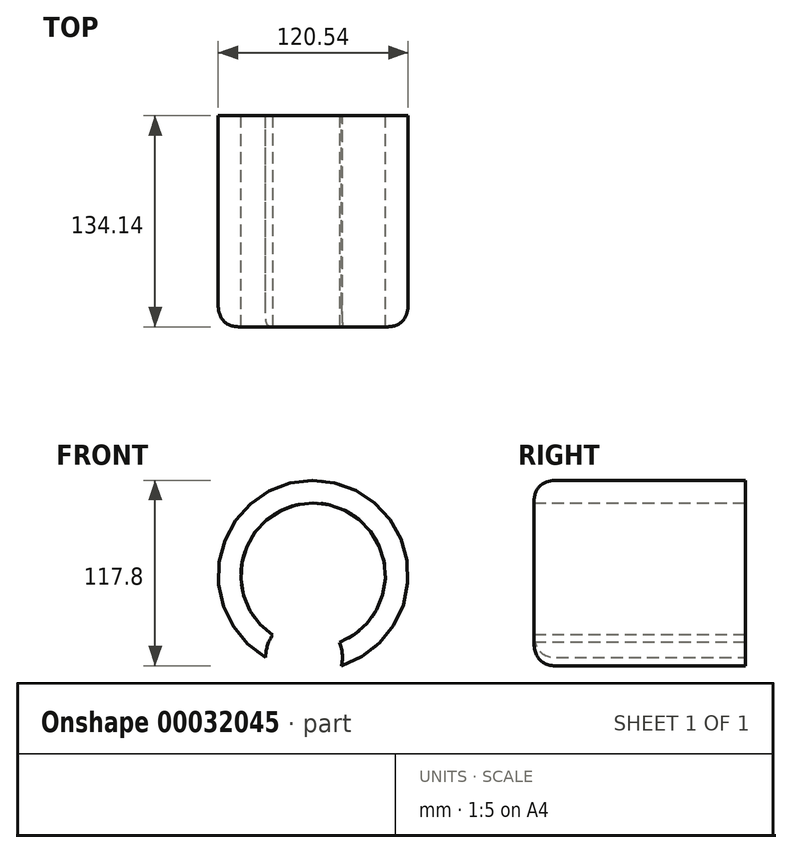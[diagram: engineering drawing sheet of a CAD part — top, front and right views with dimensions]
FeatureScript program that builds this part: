
annotation { "Feature Type Name" : "Feature", "Feature Type Description" : "" }
export const myFeature = defineFeature(function(context is Context, id is Id, definition is map)
    precondition{}
    {
        {
            var Q0;
            Q0=qCreatedBy(makeId("Front.planeOp"),FACE);
            var sketch = newSketch(context, id + "F0", { "sketchPlane" : qUnion([Q0])});
            skCircle(sketch, "E0", {"center": v(0, 0) * mm, "radius": 60.27 * mm});
            skSolve(sketch);
        }
        {
            var Q0;
            Q0=makeQuery(id+"F0.imprint","IMPRINT",FACE,{"disambiguationData":[TD([[makeQuery(id+"F0.imprint","IMPRINT",EDGE,{"derivedFrom":sQuery(id+"F0.wireOp",EDGE,"E0")}),1.0]])]});
            extrude(context, id + "F1", {"entities" : qUnion([Q0]), "depth" : 134.14 * mm});
        }
        {
            var Q0;
            Q0=makeQuery(id+"F1.opExtrude","CAP_EDGE",EDGE,{"disambiguationData":[OSD([sQuery(id+"F0.wireOp",EDGE,"E0")])],"isStart":false});
            fillet(context, id + "F2", {"entities" : qUnion([Q0]), "radius" : 14.4 * mm, "tangentPropagation" : true, "rho" : 0.5, "crossSection" : FilletCrossSection.CONIC, "allowEdgeOverflow" : false});
        }
        {
            var Q0;
            Q0=makeQuery(id+"F1.opExtrude","CAP_FACE",FACE,{"disambiguationData":[OSD([sQuery(id+"F0.wireOp",EDGE,"E0")])],"isStart":false});
            var sketch = newSketch(context, id + "F3", { "sketchPlane" : qUnion([Q0])});
            skLineSegment(sketch, "E1.bottom", {"start": v(-20.42, -26.64) * mm, "end": v(20.28, -26.64) * mm});
            skLineSegment(sketch, "E1.top", {"start": v(-20.42, 0) * mm, "end": v(20.28, 0) * mm});
            skLineSegment(sketch, "E1.left", {"start": v(-20.42, -26.64) * mm, "end": v(-20.42, 0) * mm});
            skLineSegment(sketch, "E1.right", {"start": v(20.28, -26.64) * mm, "end": v(20.28, 0) * mm});
            skSolve(sketch);
        }
        {
            var Q0;
            Q0=makeQuery(id+"F3.imprint","IMPRINT",FACE,{"disambiguationData":[TD([[makeQuery(id+"F3.imprint","IMPRINT",EDGE,{"derivedFrom":sQuery(id+"F3.wireOp",EDGE,"E1.bottom")}),1.0]])]});
            extrude(context, id + "F4", {"entities" : qUnion([Q0]), "operationType" : NewBodyOperationType.REMOVE, "oppositeDirection" : true, "depth" : 156.47 * mm});
        }
        {
            var Q0;
            Q0=makeQuery(id+"F1.opExtrude","CAP_FACE",FACE,{"disambiguationData":[OSD([sQuery(id+"F0.wireOp",EDGE,"E0")])],"isStart":false});
            extrude(context, id + "F5", {"entities" : qUnion([Q0]), "operationType" : NewBodyOperationType.REMOVE, "oppositeDirection" : true, "depth" : 234.53 * mm});
        }
        {
            var Q0;
            Q0=makeQuery(id+"F1.opExtrude","CAP_FACE",FACE,{"disambiguationData":[OSD([sQuery(id+"F0.wireOp",EDGE,"E0")])],"isStart":true});
            var sketch = newSketch(context, id + "F6", { "sketchPlane" : qUnion([Q0])});
            skCircle(sketch, "E2", {"center": v(5.77, -51.96) * mm, "radius": 24.38 * mm});
            skSolve(sketch);
        }
        {
            var Q0;
            {var subQ0=makeQuery(id+"F1.opExtrude","CAP_EDGE",EDGE,{"disambiguationData":[OSD([sQuery(id+"F0.wireOp",EDGE,"E0")])],"isStart":true});var subQ1=sQuery(id+"F6.wireOp",EDGE,"E2");var subQ3=makeQuery(id+"F6.imprint","INTERSECT",VERTEX,{"disambiguationData":[OD(0.0)],"derivedFrom":[subQ0,subQ1]});Q0=makeQuery(id+"F6.imprint","IMPRINT",FACE,{"disambiguationData":[TD([[makeQuery(id+"F6.imprint","IMPRINT",EDGE,{"disambiguationData":[TD([[subQ3,-1.0]])],"derivedFrom":subQ1}),1.0]])]});}
            var Q1;
            {var subQ0=sQuery(id+"F0.wireOp",EDGE,"E0");var subQ1=makeQuery(id+"F5.boolean.opBoolean","INTERSECT",EDGE,{"derivedFrom":[makeQuery(id+"F1.opExtrude","CAP_FACE",FACE,{"disambiguationData":[OSD([subQ0])],"isStart":true}),makeQuery(id+"F5.opExtrude","SWEPT_FACE",FACE,{"disambiguationData":[OSD([subQ0])]})]});var subQ2=sQuery(id+"F6.wireOp",EDGE,"E2");var subQ4=makeQuery(id+"F6.imprint","INTERSECT",VERTEX,{"disambiguationData":[OD(0.0)],"derivedFrom":[subQ1,subQ2]});Q1=makeQuery(id+"F6.imprint","IMPRINT",FACE,{"disambiguationData":[TD([[makeQuery(id+"F6.imprint","IMPRINT",EDGE,{"disambiguationData":[TD([[subQ4,1.0]])],"derivedFrom":subQ2}),1.0]])]});}
            var Q2;
            {var subQ0=sQuery(id+"F0.wireOp",EDGE,"E0");var subQ2=sQuery(id+"F6.wireOp",EDGE,"E2");var subQ5=makeQuery(id+"F1.opExtrude","CAP_EDGE",EDGE,{"disambiguationData":[OSD([subQ0])],"isStart":true});var subQ7=makeQuery(id+"F6.imprint","INTERSECT",VERTEX,{"disambiguationData":[OD(0.0)],"derivedFrom":[subQ5,subQ2]});Q2=makeQuery(id+"F6.imprint","IMPRINT",FACE,{"disambiguationData":[TD([[makeQuery(id+"F6.imprint","IMPRINT",EDGE,{"disambiguationData":[TD([[subQ7,1.0]])],"derivedFrom":subQ5}),-1.0]])]});}
            extrude(context, id + "F7", {"entities" : qUnion([Q0, Q1, Q2]), "operationType" : NewBodyOperationType.REMOVE, "oppositeDirection" : true, "depth" : 160.47 * mm});
        }
    });
